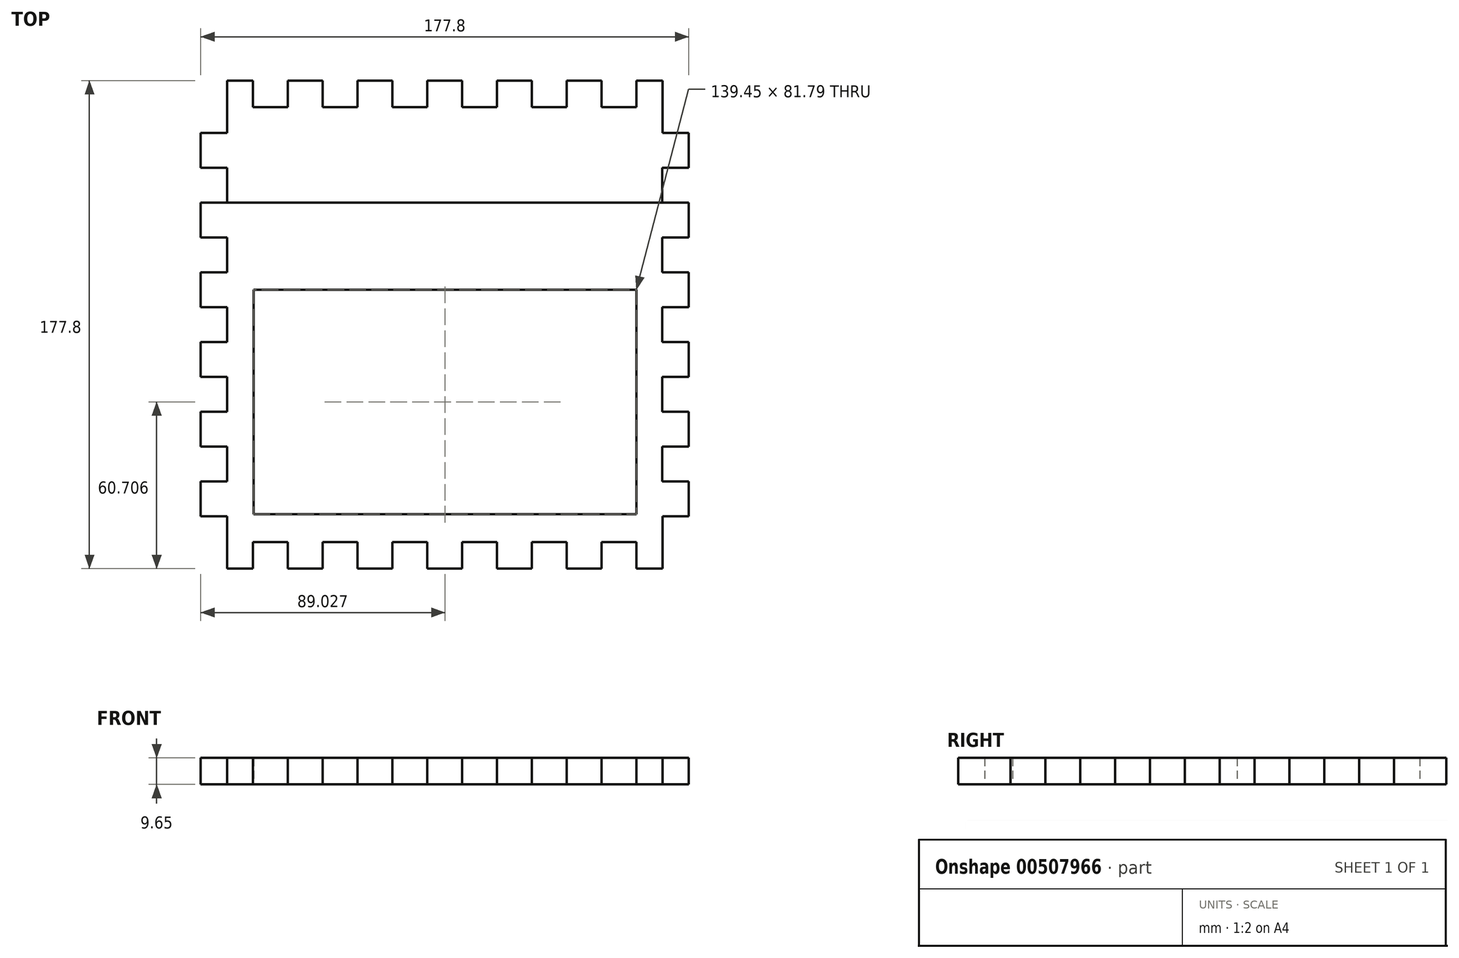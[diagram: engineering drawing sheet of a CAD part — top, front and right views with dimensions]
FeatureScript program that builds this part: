
annotation { "Feature Type Name" : "Feature", "Feature Type Description" : "" }
export const myFeature = defineFeature(function(context is Context, id is Id, definition is map)
    precondition{}
    {
        {
            var Q0;
            Q0=qCreatedBy(makeId("Top.planeOp"),FACE);
            var sketch = newSketch(context, id + "F0", { "sketchPlane" : qUnion([Q0])});
            skLineSegment(sketch, "E0.bottom", {"start": v(9.65, 0) * mm, "end": v(19.05, 0) * mm});
            skLineSegment(sketch, "E0.left", {"start": v(0, -19.05) * mm, "end": v(0, -31.75) * mm});
            skLineSegment(sketch, "E1", {"start": v(0, -19.05) * mm, "end": v(9.65, -19.05) * mm});
            skLineSegment(sketch, "E2", {"start": v(9.65, -19.05) * mm, "end": v(9.65, 0) * mm});
            skPoint(sketch, "E3.orphan", {"position": v(0, 0) * mm});
            skLineSegment(sketch, "E4", {"start": v(19.05, 0) * mm, "end": v(19.05, -9.65) * mm});
            skLineSegment(sketch, "E5", {"start": v(19.05, -9.65) * mm, "end": v(31.75, -9.65) * mm});
            skLineSegment(sketch, "E6", {"start": v(31.75, -9.65) * mm, "end": v(31.75, 0) * mm});
            skLineSegment(sketch, "E7", {"start": v(31.75, 0) * mm, "end": v(44.45, 0) * mm});
            skLineSegment(sketch, "E8", {"start": v(44.45, 0) * mm, "end": v(44.45, -9.65) * mm});
            skLineSegment(sketch, "E9", {"start": v(44.45, -9.65) * mm, "end": v(57.15, -9.65) * mm});
            skLineSegment(sketch, "E10", {"start": v(57.15, -9.65) * mm, "end": v(57.15, 0) * mm});
            skLineSegment(sketch, "E11", {"start": v(57.15, 0) * mm, "end": v(69.85, 0) * mm});
            skLineSegment(sketch, "E12", {"start": v(69.85, 0) * mm, "end": v(69.85, -9.65) * mm});
            skLineSegment(sketch, "E13", {"start": v(69.85, -9.65) * mm, "end": v(82.55, -9.65) * mm});
            skLineSegment(sketch, "E14", {"start": v(82.55, -9.65) * mm, "end": v(82.55, 0) * mm});
            skLineSegment(sketch, "E15.trimOffspring", {"start": v(82.55, 0) * mm, "end": v(95.25, 0) * mm});
            skLineSegment(sketch, "E16", {"start": v(95.25, 0) * mm, "end": v(95.25, -9.65) * mm});
            skLineSegment(sketch, "E17", {"start": v(95.25, -9.65) * mm, "end": v(107.95, -9.65) * mm});
            skLineSegment(sketch, "E18", {"start": v(107.95, -9.65) * mm, "end": v(107.95, 0) * mm});
            skLineSegment(sketch, "E19", {"start": v(107.95, 0) * mm, "end": v(120.65, 0) * mm});
            skLineSegment(sketch, "E20", {"start": v(120.65, 0) * mm, "end": v(120.65, -9.65) * mm});
            skLineSegment(sketch, "E21", {"start": v(120.65, -9.65) * mm, "end": v(133.35, -9.65) * mm});
            skLineSegment(sketch, "E22", {"start": v(133.35, -9.65) * mm, "end": v(133.35, 0) * mm});
            skLineSegment(sketch, "E23", {"start": v(133.35, 0) * mm, "end": v(146.05, 0) * mm});
            skLineSegment(sketch, "E24", {"start": v(146.05, 0) * mm, "end": v(146.05, -9.65) * mm});
            skLineSegment(sketch, "E25", {"start": v(146.05, -9.65) * mm, "end": v(158.75, -9.65) * mm});
            skLineSegment(sketch, "E26", {"start": v(158.75, -9.65) * mm, "end": v(158.75, 0) * mm});
            skLineSegment(sketch, "E27.trimOffspring", {"start": v(158.75, 0) * mm, "end": v(168.27, 0) * mm});
            skLineSegment(sketch, "E28", {"start": v(168.27, 0) * mm, "end": v(168.27, -19.05) * mm});
            skLineSegment(sketch, "E29", {"start": v(168.28, -19.05) * mm, "end": v(177.8, -19.05) * mm});
            skPoint(sketch, "E30.orphan", {"position": v(177.8, 0) * mm});
            skLineSegment(sketch, "E31", {"start": v(0, -31.75) * mm, "end": v(9.65, -31.75) * mm});
            skLineSegment(sketch, "E32", {"start": v(9.65, -31.75) * mm, "end": v(9.65, -44.45) * mm});
            skLineSegment(sketch, "E33", {"start": v(9.65, -44.45) * mm, "end": v(0, -44.45) * mm});
            skLineSegment(sketch, "E34", {"start": v(0, -44.45) * mm, "end": v(0, -57.15) * mm});
            skLineSegment(sketch, "E35", {"start": v(0, -57.15) * mm, "end": v(9.65, -57.15) * mm});
            skLineSegment(sketch, "E36", {"start": v(9.65, -57.15) * mm, "end": v(9.65, -69.85) * mm});
            skLineSegment(sketch, "E37", {"start": v(9.65, -69.85) * mm, "end": v(0, -69.85) * mm});
            skLineSegment(sketch, "E38", {"start": v(0, -69.85) * mm, "end": v(0, -82.55) * mm});
            skLineSegment(sketch, "E39", {"start": v(0, -82.55) * mm, "end": v(9.65, -82.55) * mm});
            skLineSegment(sketch, "E40", {"start": v(9.65, -82.55) * mm, "end": v(9.65, -95.25) * mm});
            skLineSegment(sketch, "E41", {"start": v(9.65, -95.25) * mm, "end": v(0, -95.25) * mm});
            skLineSegment(sketch, "E42", {"start": v(0, -95.25) * mm, "end": v(0, -107.95) * mm});
            skLineSegment(sketch, "E43", {"start": v(0, -107.95) * mm, "end": v(9.65, -107.95) * mm});
            skLineSegment(sketch, "E44", {"start": v(9.65, -107.95) * mm, "end": v(9.65, -120.65) * mm});
            skLineSegment(sketch, "E45", {"start": v(9.65, -120.65) * mm, "end": v(0, -120.65) * mm});
            skLineSegment(sketch, "E46.trimOffspring", {"start": v(0, -120.65) * mm, "end": v(0, -133.35) * mm});
            skLineSegment(sketch, "E47", {"start": v(0, -133.35) * mm, "end": v(9.65, -133.35) * mm});
            skLineSegment(sketch, "E48", {"start": v(9.65, -133.35) * mm, "end": v(9.65, -146.05) * mm});
            skLineSegment(sketch, "E49", {"start": v(9.65, -146.05) * mm, "end": v(0, -146.05) * mm});
            skLineSegment(sketch, "E50", {"start": v(0, -146.05) * mm, "end": v(0, -158.75) * mm});
            skLineSegment(sketch, "E51", {"start": v(0, -158.75) * mm, "end": v(9.65, -158.75) * mm});
            skPoint(sketch, "E0.top.start.orphan", {"position": v(0, -177.8) * mm});
            skLineSegment(sketch, "E52", {"start": v(9.65, -158.75) * mm, "end": v(9.65, -177.8) * mm});
            skLineSegment(sketch, "E53", {"start": v(88.9, 0) * mm, "end": v(88.9, -44.81) * mm, "construction": true});
            skLineSegment(sketch, "E54", {"start": v(9.65, -88.9) * mm, "end": v(71.71, -88.9) * mm, "construction": true});
            skLineSegment(sketch, "E55.MirrorCS", {"start": v(9.65, -177.8) * mm, "end": v(19.05, -177.8) * mm});
            skLineSegment(sketch, "E56.MirrorCS", {"start": v(19.05, -177.8) * mm, "end": v(19.05, -168.15) * mm});
            skLineSegment(sketch, "E57.MirrorCS", {"start": v(19.05, -168.15) * mm, "end": v(31.75, -168.15) * mm});
            skLineSegment(sketch, "E58.MirrorCS", {"start": v(31.75, -168.15) * mm, "end": v(31.75, -177.8) * mm});
            skLineSegment(sketch, "E59.MirrorCS", {"start": v(31.75, -177.8) * mm, "end": v(44.45, -177.8) * mm});
            skLineSegment(sketch, "E60.MirrorCS", {"start": v(44.45, -177.8) * mm, "end": v(44.45, -168.15) * mm});
            skLineSegment(sketch, "E61.MirrorCS", {"start": v(44.45, -168.15) * mm, "end": v(57.15, -168.15) * mm});
            skLineSegment(sketch, "E62.MirrorCS", {"start": v(57.15, -168.15) * mm, "end": v(57.15, -177.8) * mm});
            skLineSegment(sketch, "E63.MirrorCS", {"start": v(57.15, -177.8) * mm, "end": v(69.85, -177.8) * mm});
            skLineSegment(sketch, "E64.MirrorCS", {"start": v(69.85, -177.8) * mm, "end": v(69.85, -168.15) * mm});
            skLineSegment(sketch, "E65.MirrorCS", {"start": v(69.85, -168.15) * mm, "end": v(82.55, -168.15) * mm});
            skLineSegment(sketch, "E66.MirrorCS", {"start": v(82.55, -168.15) * mm, "end": v(82.55, -177.8) * mm});
            skLineSegment(sketch, "E67.MirrorCS", {"start": v(82.55, -177.8) * mm, "end": v(95.25, -177.8) * mm});
            skLineSegment(sketch, "E68.MirrorCS", {"start": v(95.25, -177.8) * mm, "end": v(95.25, -168.15) * mm});
            skLineSegment(sketch, "E69.MirrorCS", {"start": v(95.25, -168.15) * mm, "end": v(107.95, -168.15) * mm});
            skLineSegment(sketch, "E70.MirrorCS", {"start": v(107.95, -168.15) * mm, "end": v(107.95, -177.8) * mm});
            skLineSegment(sketch, "E71.MirrorCS", {"start": v(107.95, -177.8) * mm, "end": v(120.65, -177.8) * mm});
            skLineSegment(sketch, "E72.MirrorCS", {"start": v(120.65, -177.8) * mm, "end": v(120.65, -168.15) * mm});
            skLineSegment(sketch, "E73.MirrorCS", {"start": v(120.65, -168.15) * mm, "end": v(133.35, -168.15) * mm});
            skLineSegment(sketch, "E74.MirrorCS", {"start": v(133.35, -168.15) * mm, "end": v(133.35, -177.8) * mm});
            skLineSegment(sketch, "E75.MirrorCS", {"start": v(133.35, -177.8) * mm, "end": v(146.05, -177.8) * mm});
            skLineSegment(sketch, "E76.MirrorCS", {"start": v(146.05, -177.8) * mm, "end": v(146.05, -168.15) * mm});
            skLineSegment(sketch, "E77.MirrorCS", {"start": v(146.05, -168.15) * mm, "end": v(158.75, -168.15) * mm});
            skLineSegment(sketch, "E78.MirrorCS", {"start": v(158.75, -168.15) * mm, "end": v(158.75, -177.8) * mm});
            skLineSegment(sketch, "E79.MirrorCS", {"start": v(158.75, -177.8) * mm, "end": v(168.27, -177.8) * mm});
            skLineSegment(sketch, "E80.MirrorCS", {"start": v(168.27, -177.8) * mm, "end": v(168.27, -158.75) * mm});
            skLineSegment(sketch, "E81.MirrorCS", {"start": v(177.8, -19.05) * mm, "end": v(177.8, -31.75) * mm});
            skLineSegment(sketch, "E82.MirrorCS", {"start": v(177.8, -31.75) * mm, "end": v(168.15, -31.75) * mm});
            skLineSegment(sketch, "E83.MirrorCS", {"start": v(168.15, -31.75) * mm, "end": v(168.15, -44.45) * mm});
            skLineSegment(sketch, "E84.MirrorCS", {"start": v(168.15, -44.45) * mm, "end": v(177.8, -44.45) * mm});
            skLineSegment(sketch, "E85.MirrorCS", {"start": v(177.8, -44.45) * mm, "end": v(177.8, -57.15) * mm});
            skLineSegment(sketch, "E86.MirrorCS", {"start": v(177.8, -57.15) * mm, "end": v(168.15, -57.15) * mm});
            skLineSegment(sketch, "E87.MirrorCS", {"start": v(168.15, -57.15) * mm, "end": v(168.15, -69.85) * mm});
            skLineSegment(sketch, "E88.MirrorCS", {"start": v(168.15, -69.85) * mm, "end": v(177.8, -69.85) * mm});
            skLineSegment(sketch, "E89.MirrorCS", {"start": v(177.8, -69.85) * mm, "end": v(177.8, -82.55) * mm});
            skLineSegment(sketch, "E90.MirrorCS", {"start": v(177.8, -82.55) * mm, "end": v(168.15, -82.55) * mm});
            skLineSegment(sketch, "E91.MirrorCS", {"start": v(168.15, -82.55) * mm, "end": v(168.15, -95.25) * mm});
            skLineSegment(sketch, "E92.MirrorCS", {"start": v(168.15, -95.25) * mm, "end": v(177.8, -95.25) * mm});
            skLineSegment(sketch, "E93.MirrorCS", {"start": v(177.8, -95.25) * mm, "end": v(177.8, -107.95) * mm});
            skLineSegment(sketch, "E94.MirrorCS", {"start": v(177.8, -107.95) * mm, "end": v(168.15, -107.95) * mm});
            skLineSegment(sketch, "E95.MirrorCS", {"start": v(168.15, -107.95) * mm, "end": v(168.15, -120.65) * mm});
            skLineSegment(sketch, "E96.MirrorCS", {"start": v(168.15, -120.65) * mm, "end": v(177.8, -120.65) * mm});
            skLineSegment(sketch, "E97.MirrorCS", {"start": v(177.8, -120.65) * mm, "end": v(177.8, -133.35) * mm});
            skLineSegment(sketch, "E98.MirrorCS", {"start": v(177.8, -133.35) * mm, "end": v(168.15, -133.35) * mm});
            skLineSegment(sketch, "E99.MirrorCS", {"start": v(168.15, -133.35) * mm, "end": v(168.15, -146.05) * mm});
            skLineSegment(sketch, "E100.MirrorCS", {"start": v(168.15, -146.05) * mm, "end": v(177.8, -146.05) * mm});
            skLineSegment(sketch, "E101.MirrorCS", {"start": v(177.8, -146.05) * mm, "end": v(177.8, -158.75) * mm});
            skLineSegment(sketch, "E102.MirrorCS", {"start": v(177.8, -158.75) * mm, "end": v(168.15, -158.75) * mm});
            skLineSegment(sketch, "E103", {"start": v(9.65, -44.45) * mm, "end": v(168.15, -44.45) * mm});
            skLineSegment(sketch, "E104", {"start": v(0, 0) * mm, "end": v(9.65, 0) * mm, "construction": true});
            skLineSegment(sketch, "E105", {"start": v(0, 0) * mm, "end": v(0, -19.05) * mm, "construction": true});
            skLineSegment(sketch, "E106.bottom", {"start": v(19.3, -76.2) * mm, "end": v(158.75, -76.2) * mm});
            skLineSegment(sketch, "E106.top", {"start": v(19.3, -157.99) * mm, "end": v(158.75, -157.99) * mm});
            skLineSegment(sketch, "E106.left", {"start": v(19.3, -76.2) * mm, "end": v(19.3, -157.99) * mm});
            skLineSegment(sketch, "E106.right", {"start": v(158.75, -76.2) * mm, "end": v(158.75, -157.99) * mm});
            skSolve(sketch);
        }
        {
            var Q0;
            Q0=makeQuery(id+"F0.imprint","IMPRINT",FACE,{"disambiguationData":[TD([[makeQuery(id+"F0.imprint","IMPRINT",EDGE,{"derivedFrom":sQuery(id+"F0.wireOp",EDGE,"E33")}),1.0]])]});
            extrude(context, id + "F1", {"entities" : qUnion([Q0]), "depth" : 9.65 * mm});
        }
        {
            var Q0;
            Q0=makeQuery(id+"F0.imprint","IMPRINT",FACE,{"disambiguationData":[TD([[makeQuery(id+"F0.imprint","IMPRINT",EDGE,{"derivedFrom":sQuery(id+"F0.wireOp",EDGE,"E1")}),-1.0]])]});
            extrude(context, id + "F2", {"entities" : qUnion([Q0]), "depth" : 9.65 * mm});
        }
    });
